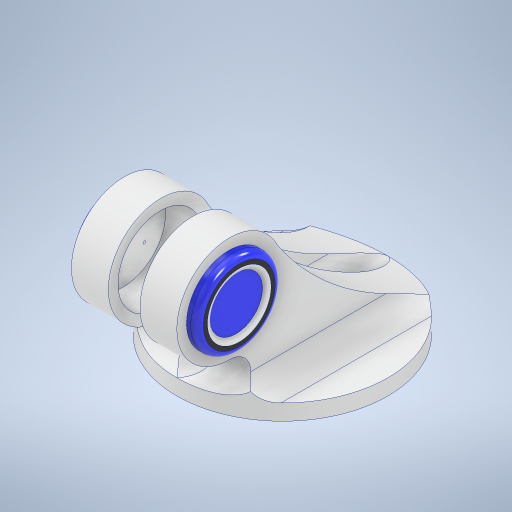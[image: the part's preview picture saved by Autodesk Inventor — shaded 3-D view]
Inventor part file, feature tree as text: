
AUTODESK INVENTOR PART (.ipt)
format: ipt  version: 2024 (Build 280153000, 153)  size: 450,560 bytes
history: native  units: mm
features: extrude x11, sketch x9, fillet x4, mirror x3
ambient origin geometry x8: Origin, YZ Plane, XZ Plane, XY Plane, X Axis, Y Axis, Z Axis, Center Point
bodies: Solid1 (feature_tree)
feature tree (27):
  sketch  "Sketch1"  dims[d0=166.0mm d1=200.0mm]
  extrude  "Extrusion1"  Depth=200.0mm
  extrude  "Extrusion2"  Depth=10.0mm TaperAngle=0.0deg
  extrude  "Extrusion3"  Depth=100.0mm
  extrude  "Extrusion4"  Depth=50.0mm
  extrude  "Extrusion5"  Depth=20.0mm TaperAngle=0.0deg
  sketch  "Sketch5"  dims[d22=20.0mm d23=50.0mm d24=0.0mm]
  extrude  "Extrusion6"  Depth=20.0mm
  extrude  "Extrusion7"  Depth=45.0mm TaperAngle=0.0deg
  fillet  "Fillet3"  Radius=50.0mm
  extrude  "Extrusion8"  Depth=7.0mm TaperAngle=0.0deg
  extrude  "Extrusion9"  Depth=6.0mm
  mirror  "Mirror1"
  extrude  "Extrusion10"  TaperAngle=0.0deg  [1 undecoded]
  mirror  "Mirror2"
  extrude  "Extrusion11"  Depth=6.0mm
  fillet  "Fillet4"  Radius=2.5mm
  fillet  "Fillet5"  Radius=5.0mm
  mirror  "Mirror3"
  fillet  "Fillet6"  Radius=20.0mm
  sketch  "Sketch2"  dims[d2=15.0mm d3=0.0mm d4=10.0mm d5=0.0mm]
  sketch  "Sketch3"  dims[d15=40.0mm d19=100.0mm]
  sketch  "Sketch4"  dims[d20=50.0mm d21=50.0mm]
  sketch  "Sketch6"  dims[d25=20.0mm d26=0.0mm d29=80.0mm]
  sketch  "Sketch7"  dims[d30=0.0mm d31=45.0mm d32=0.0mm d33=50.0mm]
  sketch  "Sketch8"  dims[d34=10.0mm d35=0.0mm d36=7.0mm d37=0.0mm]
  sketch  "Sketch9"  dims[d38=6.0mm d40=2.5mm d41=0.0mm d42=6.0mm d44=2.5mm d45=5.0mm d46=0.0mm d48=20.0mm d49=20.0mm d50=90.0mm d51=45.0mm d52=0.0mm d53=15.0mm d54=300.0mm d55=0.0mm d56=250.0mm d57=200.0mm d58=20.0mm d59=0.0mm d60=20.0mm d61=15.0mm d62=6.0mm]
note: 1 required parameter value undecoded (feature->parameter linkage not recoverable at this tier; creation-order binding heuristic only, values carry confidence <= 0.55)
